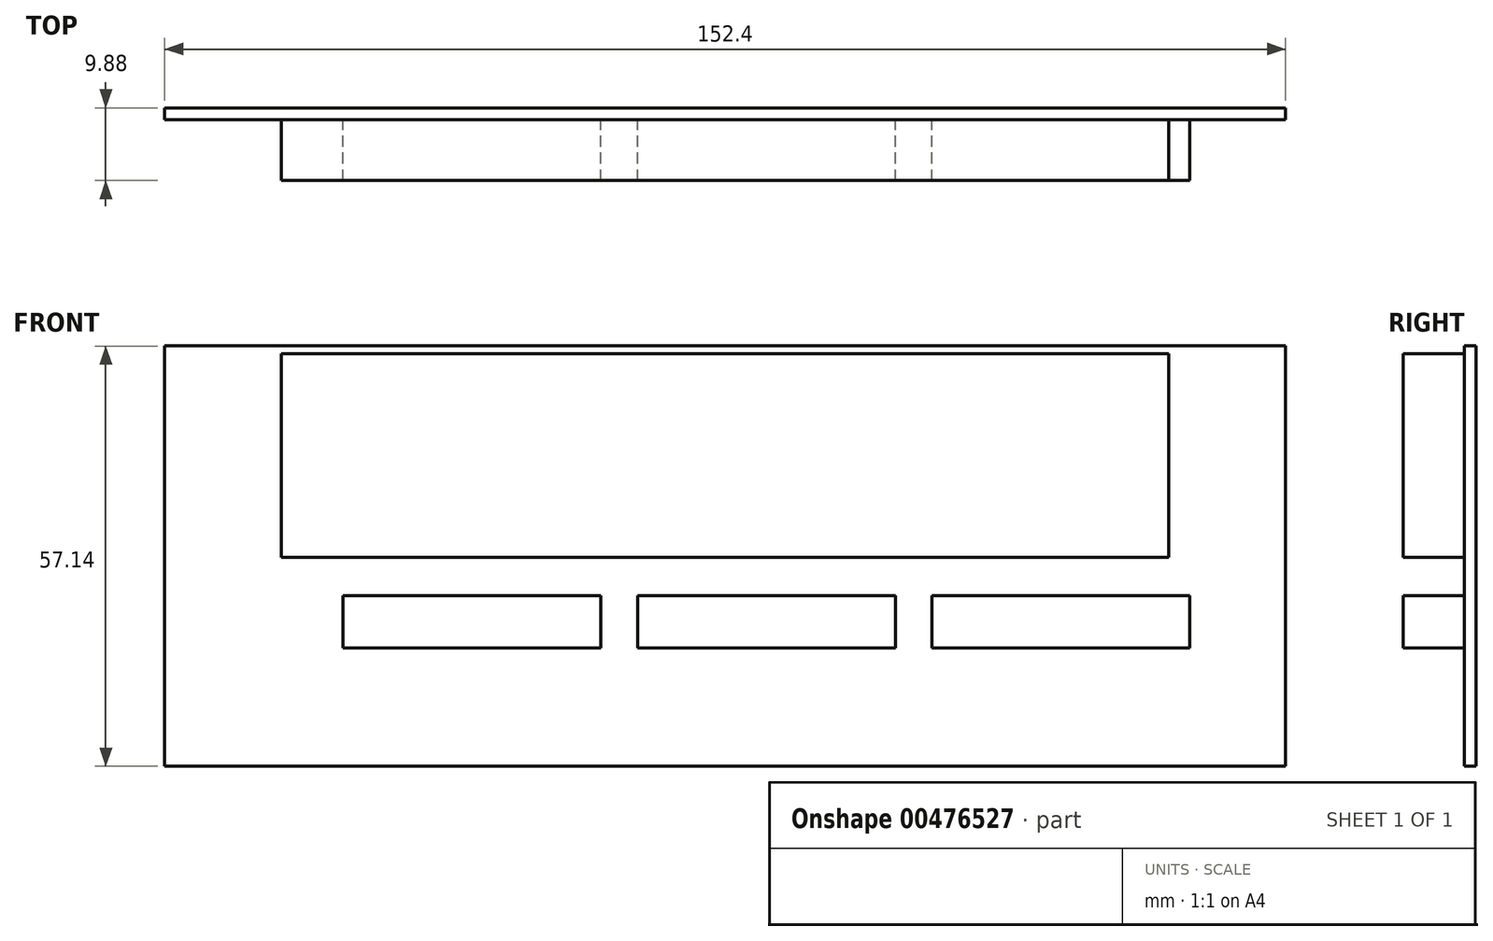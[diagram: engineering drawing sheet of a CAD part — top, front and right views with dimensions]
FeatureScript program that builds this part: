
annotation { "Feature Type Name" : "Feature", "Feature Type Description" : "" }
export const myFeature = defineFeature(function(context is Context, id is Id, definition is map)
    precondition{}
    {
        {
            var Q0;
            Q0=qCreatedBy(makeId("Front.planeOp"),FACE);
            var sketch = newSketch(context, id + "F0", { "sketchPlane" : qUnion([Q0])});
            skLineSegment(sketch, "E0.bottom", {"start": v(76.2, 28.58) * mm, "end": v(-76.2, 28.58) * mm});
            skLineSegment(sketch, "E0.top", {"start": v(76.2, -28.57) * mm, "end": v(-76.2, -28.57) * mm});
            skLineSegment(sketch, "E0.left", {"start": v(76.2, 28.58) * mm, "end": v(76.2, -28.57) * mm});
            skLineSegment(sketch, "E0.right", {"start": v(-76.2, 28.58) * mm, "end": v(-76.2, -28.57) * mm});
            skPoint(sketch, "E0.middle", {"position": v(0, 0) * mm});
            skSolve(sketch);
        }
        {
            var Q0;
            Q0 = qSketchRegion(id + "F0", true);
            extrude(context, id + "F1", {"entities" : qUnion([Q0]), "depth" : 1.6 * mm});
        }
        {
            var Q0;
            Q0=makeQuery(id+"F1.opExtrude","CAP_FACE",FACE,{"disambiguationData":[OSD([sQuery(id+"F0.wireOp",EDGE,"E0.bottom"),sQuery(id+"F0.wireOp",EDGE,"E0.top"),sQuery(id+"F0.wireOp",EDGE,"E0.left"),sQuery(id+"F0.wireOp",EDGE,"E0.right")])],"isStart":false});
            var sketch = newSketch(context, id + "F2", { "sketchPlane" : qUnion([Q0])});
            skLineSegment(sketch, "E1.bottom", {"start": v(60.33, 27.5) * mm, "end": v(-60.33, 27.5) * mm});
            skLineSegment(sketch, "E1.top", {"start": v(60.33, -0.18) * mm, "end": v(-60.33, -0.18) * mm});
            skLineSegment(sketch, "E1.left", {"start": v(60.33, 27.5) * mm, "end": v(60.32, -0.18) * mm});
            skLineSegment(sketch, "E1.right", {"start": v(-60.33, 27.5) * mm, "end": v(-60.33, -0.18) * mm});
            skPoint(sketch, "E1.middle", {"position": v(0, 13.67) * mm});
            skLineSegment(sketch, "E2", {"start": v(0, 0) * mm, "end": v(0, 13.67) * mm, "construction": true});
            skLineSegment(sketch, "E3.bottom", {"start": v(-51.94, -5.38) * mm, "end": v(-16.9, -5.38) * mm});
            skLineSegment(sketch, "E3.top", {"start": v(-51.94, -12.5) * mm, "end": v(-16.9, -12.5) * mm});
            skLineSegment(sketch, "E3.left", {"start": v(-51.94, -5.38) * mm, "end": v(-51.94, -12.5) * mm});
            skLineSegment(sketch, "E3.right", {"start": v(-16.9, -5.38) * mm, "end": v(-16.9, -12.5) * mm});
            skLineSegment(sketch, "E4.1.0.0", {"start": v(-11.92, -5.38) * mm, "end": v(23.13, -5.38) * mm});
            skLineSegment(sketch, "E4.1.0.1", {"start": v(-11.92, -5.38) * mm, "end": v(-11.92, -12.5) * mm});
            skLineSegment(sketch, "E4.1.0.2", {"start": v(-11.92, -12.5) * mm, "end": v(23.13, -12.5) * mm});
            skLineSegment(sketch, "E4.1.0.3", {"start": v(23.13, -5.38) * mm, "end": v(23.13, -12.5) * mm});
            skLineSegment(sketch, "E4.2.0.0", {"start": v(28.1, -5.38) * mm, "end": v(63.15, -5.38) * mm});
            skLineSegment(sketch, "E4.2.0.1", {"start": v(28.1, -5.38) * mm, "end": v(28.1, -12.5) * mm});
            skLineSegment(sketch, "E4.2.0.2", {"start": v(28.1, -12.5) * mm, "end": v(63.15, -12.5) * mm});
            skLineSegment(sketch, "E4.2.0.3", {"start": v(63.15, -5.38) * mm, "end": v(63.15, -12.5) * mm});
            skLineSegment(sketch, "E4.direction1", {"start": v(-51.94, -5.38) * mm, "end": v(-11.92, -5.38) * mm, "construction": true});
            skSolve(sketch);
        }
        {
            var Q0;
            Q0 = qSketchRegion(id + "F2", true);
            extrude(context, id + "F3", {"entities" : qUnion([Q0]), "operationType" : NewBodyOperationType.ADD, "depth" : 8.28 * mm});
        }
    });
